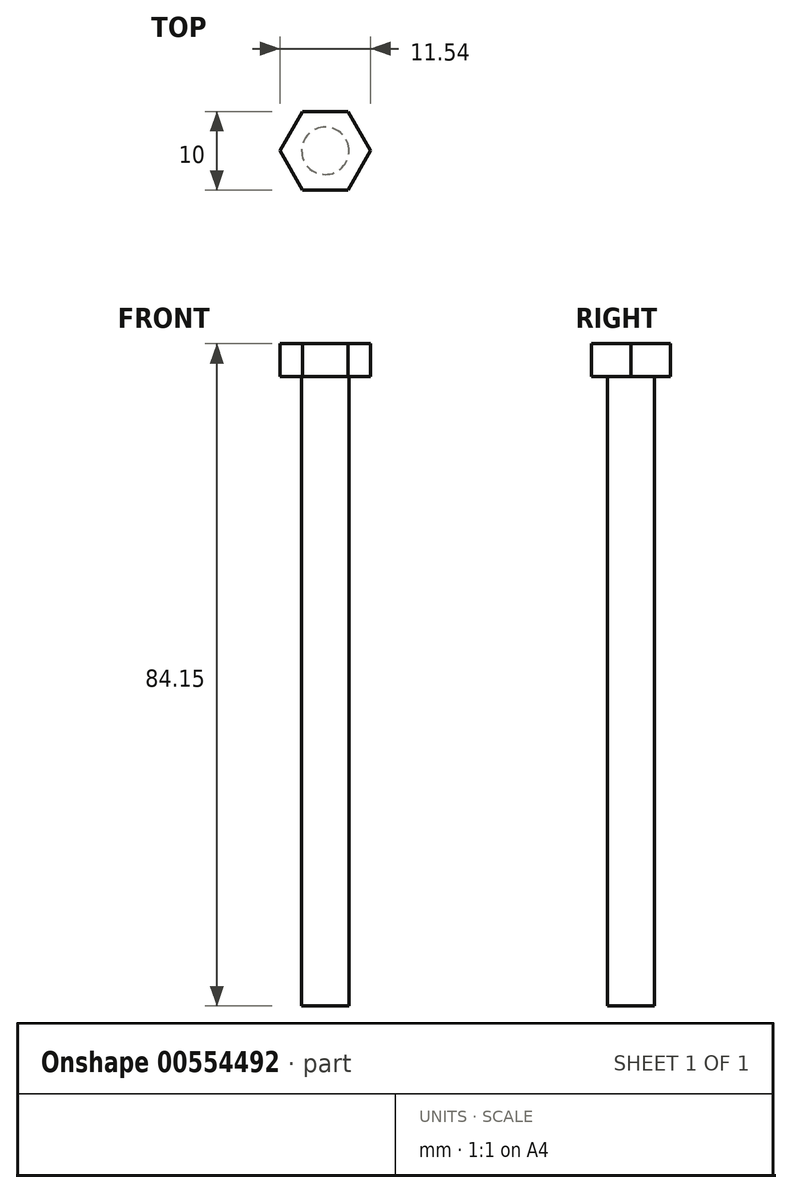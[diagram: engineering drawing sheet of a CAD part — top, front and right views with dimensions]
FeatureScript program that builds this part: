
annotation { "Feature Type Name" : "Feature", "Feature Type Description" : "" }
export const myFeature = defineFeature(function(context is Context, id is Id, definition is map)
    precondition{}
    {
        {
            var Q0;
            Q0=qCreatedBy(makeId("Top.planeOp"),FACE);
            var sketch = newSketch(context, id + "F0", { "sketchPlane" : qUnion([Q0])});
            skCircle(sketch, "E0.cCircle", {"center": v(0, 0) * mm, "radius": 5 * mm, "construction": true});
            skLineSegment(sketch, "E0.0", {"start": v(5.77, 0) * mm, "end": v(2.89, -5) * mm});
            skLineSegment(sketch, "E0.1", {"start": v(2.89, -5) * mm, "end": v(-2.89, -5) * mm});
            skLineSegment(sketch, "E0.2", {"start": v(-2.89, -5) * mm, "end": v(-5.77, 0) * mm});
            skLineSegment(sketch, "E0.3", {"start": v(-5.77, 0) * mm, "end": v(-2.89, 5) * mm});
            skLineSegment(sketch, "E0.4", {"start": v(-2.89, 5) * mm, "end": v(2.89, 5) * mm});
            skLineSegment(sketch, "E0.5", {"start": v(2.89, 5) * mm, "end": v(5.77, 0) * mm});
            skPoint(sketch, "E0.0.midPoint", {"position": v(4.33, -2.5) * mm});
            skSolve(sketch);
        }
        {
            var Q0;
            Q0=makeQuery(id+"F0.imprint","IMPRINT",FACE,{"disambiguationData":[TD([[makeQuery(id+"F0.imprint","IMPRINT",EDGE,{"derivedFrom":sQuery(id+"F0.wireOp",EDGE,"E0.0")}),-1.0]])]});
            extrude(context, id + "F1", {"entities" : qUnion([Q0]), "depth" : 4.15 * mm, "offsetDistance" : 25 * mm});
        }
        {
            var Q0;
            Q0=makeQuery(id+"F1.opExtrude","CAP_FACE",FACE,{"disambiguationData":[OSD([sQuery(id+"F0.wireOp",EDGE,"E0.0"),sQuery(id+"F0.wireOp",EDGE,"E0.1"),sQuery(id+"F0.wireOp",EDGE,"E0.2"),sQuery(id+"F0.wireOp",EDGE,"E0.3"),sQuery(id+"F0.wireOp",EDGE,"E0.4"),sQuery(id+"F0.wireOp",EDGE,"E0.5")])],"isStart":true});
            var sketch = newSketch(context, id + "F2", { "sketchPlane" : qUnion([Q0])});
            skCircle(sketch, "E1", {"center": v(0, 0) * mm, "radius": 3 * mm});
            skSolve(sketch);
        }
        {
            var Q0;
            Q0=makeQuery(id+"F2.imprint","IMPRINT",FACE,{"disambiguationData":[TD([[makeQuery(id+"F2.imprint","IMPRINT",EDGE,{"derivedFrom":sQuery(id+"F2.wireOp",EDGE,"E1")}),1.0]])]});
            extrude(context, id + "F3", {"entities" : qUnion([Q0]), "operationType" : NewBodyOperationType.ADD, "depth" : 80 * mm, "offsetDistance" : 25 * mm});
        }
    });
